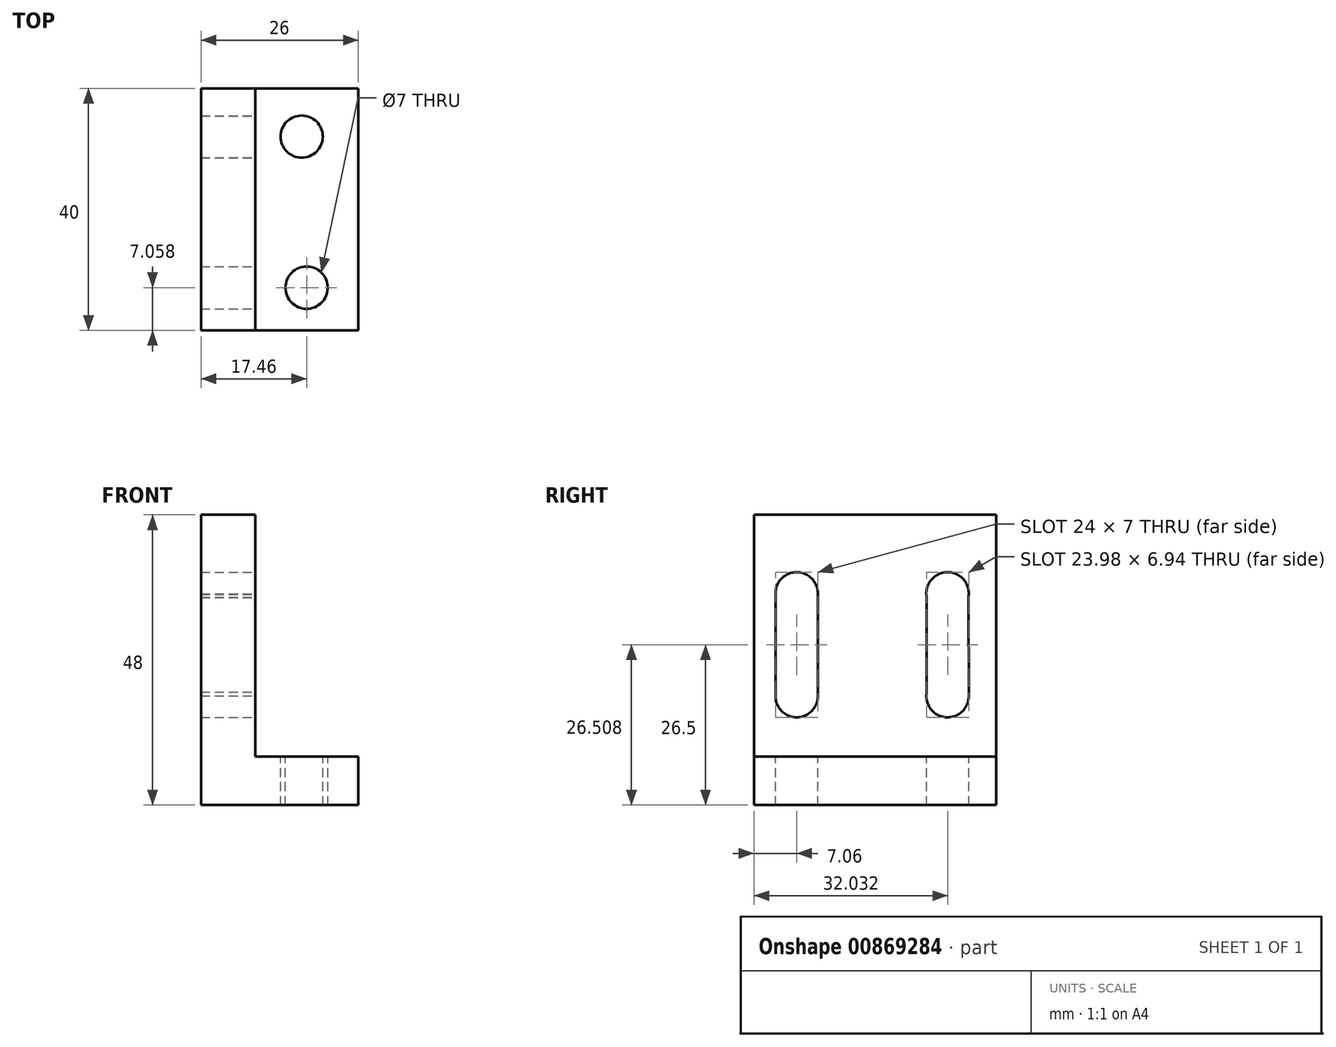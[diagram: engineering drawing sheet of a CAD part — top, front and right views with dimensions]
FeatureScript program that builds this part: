
annotation { "Feature Type Name" : "Feature", "Feature Type Description" : "" }
export const myFeature = defineFeature(function(context is Context, id is Id, definition is map)
    precondition{}
    {
        {
            var Q0;
            Q0=qCreatedBy(makeId("Front.planeOp"),FACE);
            var sketch = newSketch(context, id + "F0", { "sketchPlane" : qUnion([Q0])});
            skLineSegment(sketch, "E0.top", {"start": v(0, 40) * mm, "end": v(-9, 40) * mm});
            skLineSegment(sketch, "E0.left", {"start": v(0, 0) * mm, "end": v(0, 40) * mm});
            skLineSegment(sketch, "E0.right", {"start": v(-9, 0) * mm, "end": v(-9, 40) * mm});
            skLineSegment(sketch, "E1.bottom", {"start": v(0, 0) * mm, "end": v(17, 0) * mm});
            skLineSegment(sketch, "E1.top", {"start": v(-9, -8) * mm, "end": v(17, -8) * mm});
            skLineSegment(sketch, "E1.left", {"start": v(-9, 0) * mm, "end": v(-9, -8) * mm});
            skLineSegment(sketch, "E1.right", {"start": v(17, 0) * mm, "end": v(17, -8) * mm});
            skSolve(sketch);
        }
        {
            var Q0;
            Q0 = qSketchRegion(id + "F0", true);
            extrude(context, id + "F1", {"entities" : qUnion([Q0]), "depth" : 40 * mm, "offsetDistance" : 25 * mm});
        }
        {
            var Q0;
            Q0=makeQuery(id+"F1.opExtrude","SWEPT_FACE",FACE,{"disambiguationData":[OSD([sQuery(id+"F0.wireOp",EDGE,"E1.bottom")])]});
            var sketch = newSketch(context, id + "F2", { "sketchPlane" : qUnion([Q0])});
            skCircle(sketch, "E2", {"center": v(8.46, -32.94) * mm, "radius": 3.5 * mm});
            skCircle(sketch, "E3", {"center": v(7.65, -7.95) * mm, "radius": 3.48 * mm});
            skSolve(sketch);
        }
        {
            var Q0;
            Q0 = qSketchRegion(id + "F2", true);
            extrude(context, id + "F3", {"entities" : qUnion([Q0]), "operationType" : NewBodyOperationType.REMOVE, "oppositeDirection" : true, "depth" : 25 * mm, "offsetDistance" : 25 * mm});
        }
        {
            var Q0;
            Q0=makeQuery(id+"F1.opExtrude","SWEPT_FACE",FACE,{"disambiguationData":[OSD([sQuery(id+"F0.wireOp",EDGE,"E0.left")])]});
            var sketch = newSketch(context, id + "F4", { "sketchPlane" : qUnion([Q0])});
            skArc(sketch, "E4", {"start": v(-29.45, 26.78) * mm, "mid": v(-32.86, 30.5) * mm, "end": v(-36.44, 26.95) * mm});
            skArc(sketch, "E5", {"start": v(-36.44, 10.05) * mm, "mid": v(-32.97, 6.5) * mm, "end": v(-29.44, 10) * mm});
            skLineSegment(sketch, "E6", {"start": v(-29.45, 26.78) * mm, "end": v(-29.44, 9.65) * mm});
            skLineSegment(sketch, "E7", {"start": v(-36.44, 26.95) * mm, "end": v(-36.44, 9.95) * mm});
            skArc(sketch, "E8", {"start": v(-11.44, 10.66) * mm, "mid": v(-8.33, 6.52) * mm, "end": v(-4.5, 10.01) * mm});
            skArc(sketch, "E9", {"start": v(-4.57, 26.33) * mm, "mid": v(-8, 30.5) * mm, "end": v(-11.44, 26.34) * mm});
            skLineSegment(sketch, "E10", {"start": v(-11.44, 27.66) * mm, "end": v(-11.44, 9.34) * mm});
            skLineSegment(sketch, "E11", {"start": v(-4.57, 27.7) * mm, "end": v(-4.5, 9.34) * mm});
            skSolve(sketch);
        }
        {
            var Q0;
            Q0 = qSketchRegion(id + "F4", true);
            extrude(context, id + "F5", {"entities" : qUnion([Q0]), "operationType" : NewBodyOperationType.REMOVE, "oppositeDirection" : true, "depth" : 25 * mm, "offsetDistance" : 25 * mm});
        }
    });
